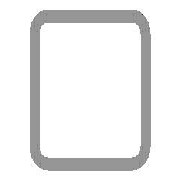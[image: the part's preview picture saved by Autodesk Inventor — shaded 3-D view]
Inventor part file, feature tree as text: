
AUTODESK INVENTOR PART (.ipt)
format: ipt  version: 2016 (Build 200138000, 138)  size: 128,512 bytes
history: native  units: mm (DEFAULTED — no unit token found)
features: other x4, sketch x3, plane x1
ambient origin geometry x8: Origin, YZ Plane, XZ Plane, XY Plane, X Axis, Y Axis, Z Axis, Center Point
bodies: Solid1 (feature_tree), Body (feature_tree)
feature tree (8):
  parser-record x1  (decoder bookkeeping rows leaked as tree rows — omitted from the tree; the rows remain in map.json)
  other  "Driven Length"
  other  "Start plane"
  other  "End plane"
  sketch  "Sketch"  dims[d7=4.0mm d9=25.0mm d11=25.0mm d12=2.0mm d13=-0.0mm d14=310.0mm d15=12.5mm d16=12.5mm d17=90.0deg d18=310.0mm]
  sketch  "Sketch3"  dims[d3=310.0mm]
  plane  "Work Plane3"
  sketch  "Sketch4"  dims[d4=0.0mm]
